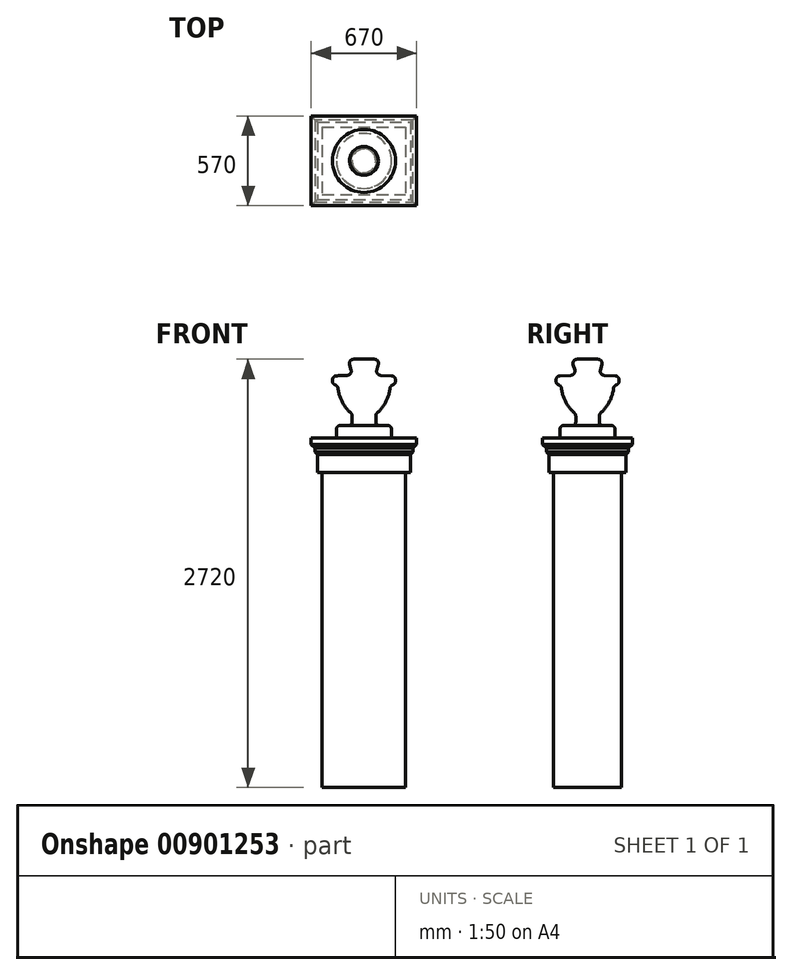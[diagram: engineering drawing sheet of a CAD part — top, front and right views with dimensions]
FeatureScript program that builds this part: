
annotation { "Feature Type Name" : "Feature", "Feature Type Description" : "" }
export const myFeature = defineFeature(function(context is Context, id is Id, definition is map)
    precondition{}
    {
        {
            var Q0;
            Q0=qCreatedBy(makeId("Top.planeOp"),FACE);
            var sketch = newSketch(context, id + "F0", { "sketchPlane" : qUnion([Q0])});
            skLineSegment(sketch, "E0.bottom", {"start": v(-265, 215) * mm, "end": v(265, 215) * mm});
            skLineSegment(sketch, "E0.top", {"start": v(-265, -215) * mm, "end": v(265, -215) * mm});
            skLineSegment(sketch, "E0.left", {"start": v(-265, 215) * mm, "end": v(-265, -215) * mm});
            skLineSegment(sketch, "E0.right", {"start": v(265, 215) * mm, "end": v(265, -215) * mm});
            skSolve(sketch);
        }
        {
            var Q0;
            Q0 = qSketchRegion(id + "F0", true);
            extrude(context, id + "F1", {"entities" : qUnion([Q0]), "depth" : 2000 * mm, "offsetDistance" : 25.4 * mm});
        }
        {
            var Q0;
            Q0=makeQuery(id+"F1.opExtrude","CAP_FACE",FACE,{"disambiguationData":[OSD([sQuery(id+"F0.wireOp",EDGE,"E0.bottom"),sQuery(id+"F0.wireOp",EDGE,"E0.top"),sQuery(id+"F0.wireOp",EDGE,"E0.left"),sQuery(id+"F0.wireOp",EDGE,"E0.right")])],"isStart":false});
            var sketch = newSketch(context, id + "F2", { "sketchPlane" : qUnion([Q0])});
            skLineSegment(sketch, "E1.bottom", {"start": v(-295, 245) * mm, "end": v(295, 245) * mm});
            skLineSegment(sketch, "E1.top", {"start": v(-295, -245) * mm, "end": v(295, -245) * mm});
            skLineSegment(sketch, "E1.left", {"start": v(-295, 245) * mm, "end": v(-295, -245) * mm});
            skLineSegment(sketch, "E1.right", {"start": v(295, 245) * mm, "end": v(295, -245) * mm});
            skSolve(sketch);
        }
        {
            var Q0;
            Q0 = qSketchRegion(id + "F2", true);
            extrude(context, id + "F3", {"entities" : qUnion([Q0]), "operationType" : NewBodyOperationType.ADD, "depth" : 100 * mm, "offsetDistance" : 25.4 * mm});
        }
        {
            var Q0;
            Q0=qCreatedBy(makeId("Right.planeOp"),FACE);
            var sketch = newSketch(context, id + "F4", { "sketchPlane" : qUnion([Q0])});
            skLineSegment(sketch, "E2.0", {"start": v(-245, 2100) * mm, "end": v(-245, 2000) * mm, "construction": true});
            skLineSegment(sketch, "E3.0", {"start": v(245, 2100) * mm, "end": v(-245, 2100) * mm, "construction": true});
            skLineSegment(sketch, "E4", {"start": v(-245, 2100) * mm, "end": v(-245, 2115) * mm});
            skLineSegment(sketch, "E5", {"start": v(-245, 2115) * mm, "end": v(-260, 2130) * mm});
            skLineSegment(sketch, "E6", {"start": v(-260, 2130) * mm, "end": v(-260, 2155) * mm});
            skLineSegment(sketch, "E7", {"start": v(-260, 2155) * mm, "end": v(-285, 2180) * mm});
            skLineSegment(sketch, "E8", {"start": v(-285, 2180) * mm, "end": v(-285, 2220) * mm});
            skLineSegment(sketch, "E9", {"start": v(-285, 2220) * mm, "end": v(-205, 2220) * mm});
            skLineSegment(sketch, "E10", {"start": v(-245, 2100) * mm, "end": v(-205, 2100) * mm});
            skLineSegment(sketch, "E11", {"start": v(-205, 2100) * mm, "end": v(-205, 2220) * mm});
            skPoint(sketch, "E12.orphan", {"position": v(-230, 2220) * mm});
            skSolve(sketch);
        }
        {
            var Q0;
            Q0 = qSketchRegion(id + "F4", true);
            var Q1;
            Q1=makeQuery(id+"F3.opExtrude","CAP_EDGE",EDGE,{"disambiguationData":[OSD([sQuery(id+"F2.wireOp",EDGE,"E1.top")])],"isStart":false});
            var Q2;
            Q2=makeQuery(id+"F3.opExtrude","CAP_EDGE",EDGE,{"disambiguationData":[OSD([sQuery(id+"F2.wireOp",EDGE,"E1.right")])],"isStart":false});
            var Q3;
            Q3=makeQuery(id+"F3.opExtrude","CAP_EDGE",EDGE,{"disambiguationData":[OSD([sQuery(id+"F2.wireOp",EDGE,"E1.bottom")])],"isStart":false});
            var Q4;
            Q4=makeQuery(id+"F3.opExtrude","CAP_EDGE",EDGE,{"disambiguationData":[OSD([sQuery(id+"F2.wireOp",EDGE,"E1.left")])],"isStart":false});
            sweep(context, id + "F5", {"profiles" : qUnion([Q0]), "path" : qUnion([Q1, Q2, Q3, Q4])});
        }
        {
            var Q0;
            Q0=makeQuery(id+"F5.opSweep","SWEPT_FACE",FACE,{"disambiguationData":[OSD([sQuery(id+"F2.wireOp",EDGE,"E1.right"),sQuery(id+"F4.wireOp",EDGE,"E9")])]});
            var sketch = newSketch(context, id + "F6", { "sketchPlane" : qUnion([Q0])});
            skLineSegment(sketch, "E13.0", {"start": v(-255, 205) * mm, "end": v(-255, -205) * mm});
            skLineSegment(sketch, "E14.0", {"start": v(-255, -205) * mm, "end": v(255, -205) * mm});
            skLineSegment(sketch, "E15.0", {"start": v(255, -205) * mm, "end": v(255, 205) * mm});
            skLineSegment(sketch, "E16.0", {"start": v(255, 205) * mm, "end": v(-255, 205) * mm});
            skSolve(sketch);
        }
        {
            var Q0;
            Q0 = qSketchRegion(id + "F6", true);
            var Q1;
            Q1=makeQuery(id+"F3.opExtrude","CAP_FACE",FACE,{"disambiguationData":[OSD([sQuery(id+"F2.wireOp",EDGE,"E1.bottom"),sQuery(id+"F2.wireOp",EDGE,"E1.top"),sQuery(id+"F2.wireOp",EDGE,"E1.left"),sQuery(id+"F2.wireOp",EDGE,"E1.right")])],"isStart":false});
            var Q2;
            Q2=makeQuery(id+"F5.opSweep","MID_CAP_VERTEX",VERTEX,{"disambiguationData":[OSD([sQuery(id+"F2.wireOp",EDGE,"E1.bottom"),sQuery(id+"F4.wireOp",EDGE,"E10"),sQuery(id+"F4.wireOp",EDGE,"E11")])],"capPos":2.0});
            extrude(context, id + "F7", {"entities" : qUnion([Q0]), "operationType" : NewBodyOperationType.ADD, "endBound" : BoundingType.UP_TO_SURFACE, "oppositeDirection" : true, "depth" : 25.4 * mm, "endBoundEntityFace" : qUnion([Q1]), "endBoundEntityVertex" : qUnion([Q2]), "offsetDistance" : 25.4 * mm});
        }
        {
            var Q0;
            Q0=qCreatedBy(makeId("Right.planeOp"),FACE);
            var sketch = newSketch(context, id + "F8", { "sketchPlane" : qUnion([Q0])});
            skLineSegment(sketch, "E17", {"start": v(0, 0) * mm, "end": v(0, 2720) * mm, "construction": true});
            skLineSegment(sketch, "E18.0", {"start": v(-285, 2220) * mm, "end": v(285, 2220) * mm, "construction": true});
            skLineSegment(sketch, "E19", {"start": v(0, 2720) * mm, "end": v(100, 2720) * mm});
            skLineSegment(sketch, "E20", {"start": v(100, 2720) * mm, "end": v(73.2, 2620) * mm});
            skLineSegment(sketch, "E21", {"start": v(73.2, 2620) * mm, "end": v(200, 2613.35) * mm});
            skLineSegment(sketch, "E22", {"start": v(200, 2613.35) * mm, "end": v(200, 2563.35) * mm});
            skLineSegment(sketch, "E23", {"start": v(200, 2563.35) * mm, "end": v(166.81, 2551.28) * mm});
            skLineSegment(sketch, "E24", {"start": v(0, 2220) * mm, "end": v(175, 2220) * mm});
            skLineSegment(sketch, "E25", {"start": v(175, 2220) * mm, "end": v(175, 2300) * mm});
            skLineSegment(sketch, "E26", {"start": v(175, 2300) * mm, "end": v(75, 2300) * mm});
            skLineSegment(sketch, "E27", {"start": v(75, 2300) * mm, "end": v(75, 2371.6) * mm});
            skArc(sketch, "E28", {"start": v(75, 2371.6) * mm, "mid": v(139.84, 2451.76) * mm, "end": v(166.81, 2551.28) * mm});
            skLineSegment(sketch, "E29", {"start": v(73.2, 2620) * mm, "end": v(128.16, 2620) * mm, "construction": true});
            skLineSegment(sketch, "E30", {"start": v(0, 2720) * mm, "end": v(0, 2220) * mm});
            skSolve(sketch);
        }
        {
            var Q0;
            Q0 = qSketchRegion(id + "F8", true);
            var Q1;
            Q1=sQuery(id+"F8.wireOp",EDGE,"E17");
            revolve(context, id + "F9", {"operationType" : NewBodyOperationType.ADD, "surfaceOperationType" : NewSurfaceOperationType.NEW, "entities" : qUnion([Q0]), "axis" : qUnion([Q1]), "revolveType" : RevolveType.FULL});
        }
        {
            var Q0;
            Q0=makeQuery(id+"F9.opRevolve","SWEPT_EDGE",EDGE,{"disambiguationData":[OSD([sQuery(id+"F8.wireOp",EDGE,"E24"),sQuery(id+"F8.wireOp",EDGE,"E25")])]});
            var Q1;
            Q1=makeQuery(id+"F9.opRevolve","SWEPT_EDGE",EDGE,{"disambiguationData":[OSD([sQuery(id+"F8.wireOp",EDGE,"E25"),sQuery(id+"F8.wireOp",EDGE,"E26")])]});
            var Q2;
            Q2=makeQuery(id+"F9.opRevolve","SWEPT_EDGE",EDGE,{"disambiguationData":[OSD([sQuery(id+"F8.wireOp",EDGE,"E27"),sQuery(id+"F8.wireOp",EDGE,"E28")])]});
            var Q3;
            Q3=makeQuery(id+"F9.opRevolve","SWEPT_EDGE",EDGE,{"disambiguationData":[OSD([sQuery(id+"F8.wireOp",EDGE,"E23"),sQuery(id+"F8.wireOp",EDGE,"E28")])]});
            var Q4;
            Q4=makeQuery(id+"F9.opRevolve","SWEPT_EDGE",EDGE,{"disambiguationData":[OSD([sQuery(id+"F8.wireOp",EDGE,"E20"),sQuery(id+"F8.wireOp",EDGE,"E21")])]});
            var Q5;
            Q5=makeQuery(id+"F9.opRevolve","SWEPT_EDGE",EDGE,{"disambiguationData":[OSD([sQuery(id+"F8.wireOp",EDGE,"E22"),sQuery(id+"F8.wireOp",EDGE,"E23")])]});
            var Q6;
            Q6=makeQuery(id+"F9.opRevolve","SWEPT_EDGE",EDGE,{"disambiguationData":[OSD([sQuery(id+"F8.wireOp",EDGE,"E21"),sQuery(id+"F8.wireOp",EDGE,"E22")])]});
            var Q7;
            Q7=makeQuery(id+"F9.opRevolve","SWEPT_EDGE",EDGE,{"disambiguationData":[OSD([sQuery(id+"F8.wireOp",EDGE,"E19"),sQuery(id+"F8.wireOp",EDGE,"E20")])]});
            fillet(context, id + "F10", {"entities" : qUnion([Q0, Q1, Q2, Q3, Q4, Q5, Q6, Q7]), "radius" : 25.4 * mm, "tangentPropagation" : true, "allowEdgeOverflow" : false});
        }
        {
            var Q0;
            Q0=makeQuery(id+"F9.opRevolve","SWEPT_EDGE",EDGE,{"disambiguationData":[OSD([sQuery(id+"F8.wireOp",EDGE,"E26"),sQuery(id+"F8.wireOp",EDGE,"E27")])]});
            fillet(context, id + "F11", {"entities" : qUnion([Q0]), "radius" : 19.05 * mm, "tangentPropagation" : true, "allowEdgeOverflow" : false});
        }
    });
